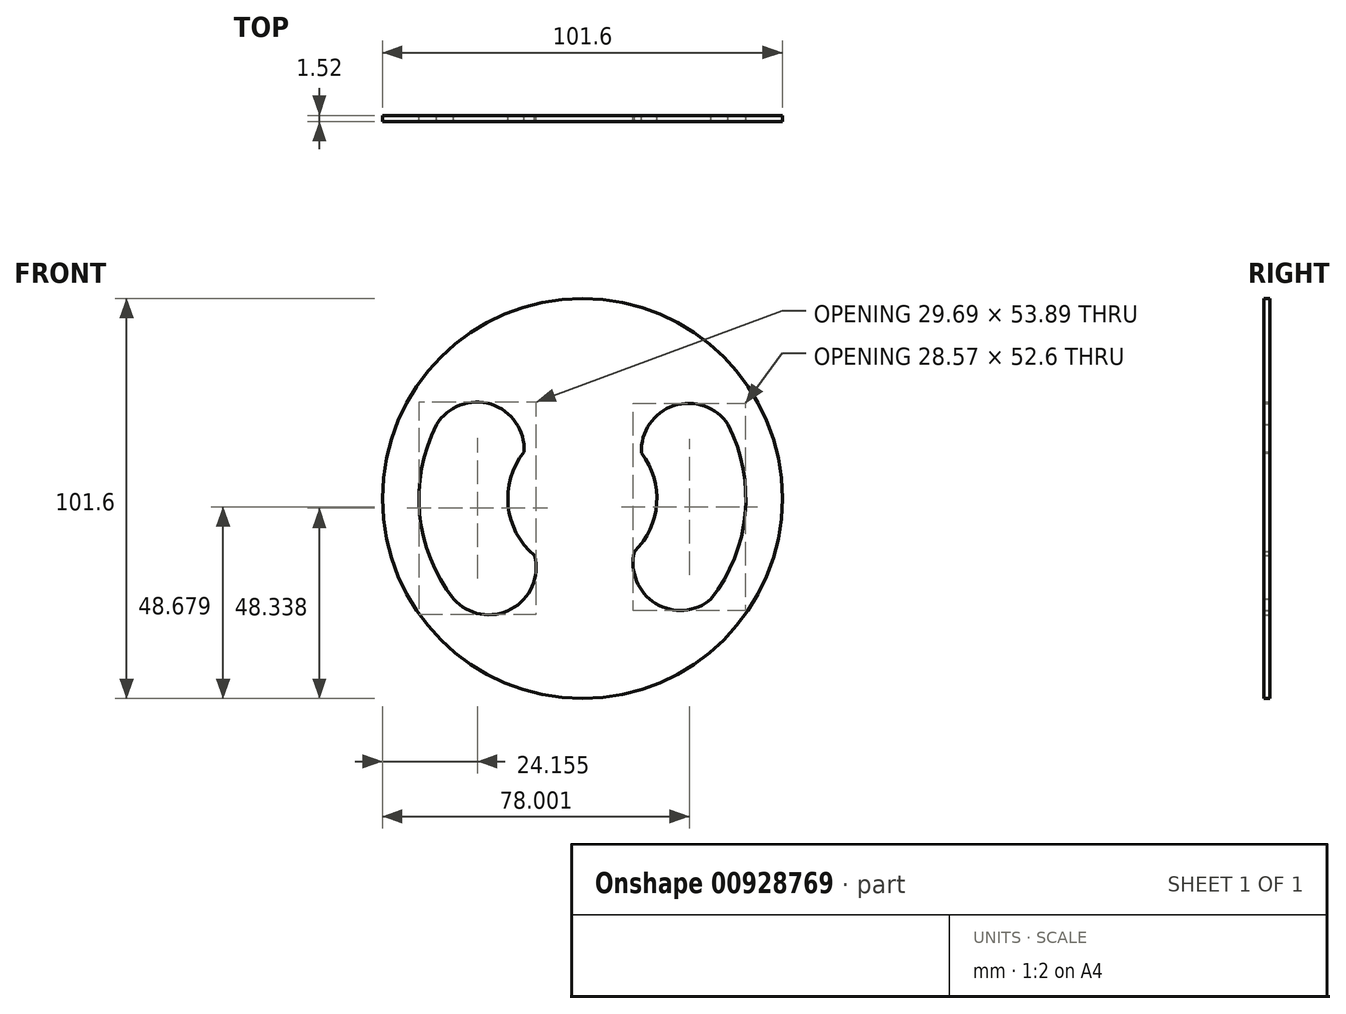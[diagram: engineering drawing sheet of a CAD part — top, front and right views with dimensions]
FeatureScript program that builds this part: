
annotation { "Feature Type Name" : "Feature", "Feature Type Description" : "" }
export const myFeature = defineFeature(function(context is Context, id is Id, definition is map)
    precondition{}
    {
        {
            var Q0;
            Q0=qCreatedBy(makeId("Front.planeOp"),FACE);
            var sketch = newSketch(context, id + "F0", { "sketchPlane" : qUnion([Q0])});
            skCircle(sketch, "E0", {"center": v(0, 0) * mm, "radius": 50.8 * mm});
            skArc(sketch, "E1", {"start": v(-37.05, 18.76) * mm, "mid": v(-41.33, -4.02) * mm, "end": v(-32.74, -25.54) * mm});
            skArc(sketch, "E2", {"start": v(13.25, -13.51) * mm, "mid": v(18.88, -1.33) * mm, "end": v(15.01, 11.52) * mm});
            skArc(sketch, "E3", {"start": v(37.05, 18.76) * mm, "mid": v(23.26, 23.58) * mm, "end": v(15.01, 11.52) * mm});
            skArc(sketch, "E4", {"start": v(-14.82, 11.77) * mm, "mid": v(-23.2, 23.94) * mm, "end": v(-37.05, 18.76) * mm});
            skArc(sketch, "E5", {"start": v(-32.74, -25.54) * mm, "mid": v(-18.1, -28.13) * mm, "end": v(-12.16, -14.5) * mm});
            skArc(sketch, "E6", {"start": v(13.25, -13.51) * mm, "mid": v(18.59, -26.67) * mm, "end": v(32.74, -25.54) * mm});
            skArc(sketch, "E7.trimOffspring", {"start": v(32.74, -25.54) * mm, "mid": v(41.33, -4.02) * mm, "end": v(37.05, 18.76) * mm});
            skArc(sketch, "E8.trimOffspring", {"start": v(-14.82, 11.77) * mm, "mid": v(-18.83, -1.9) * mm, "end": v(-12.16, -14.5) * mm});
            skSolve(sketch);
        }
        {
            var Q0;
            Q0=makeQuery(id+"F0.imprint","IMPRINT",FACE,{"disambiguationData":[TD([[makeQuery(id+"F0.imprint","IMPRINT",EDGE,{"derivedFrom":sQuery(id+"F0.wireOp",EDGE,"E0")}),1.0]])]});
            extrude(context, id + "F1", {"entities" : qUnion([Q0]), "depth" : 1.52 * mm, "offsetDistance" : 25.4 * mm});
        }
    });
